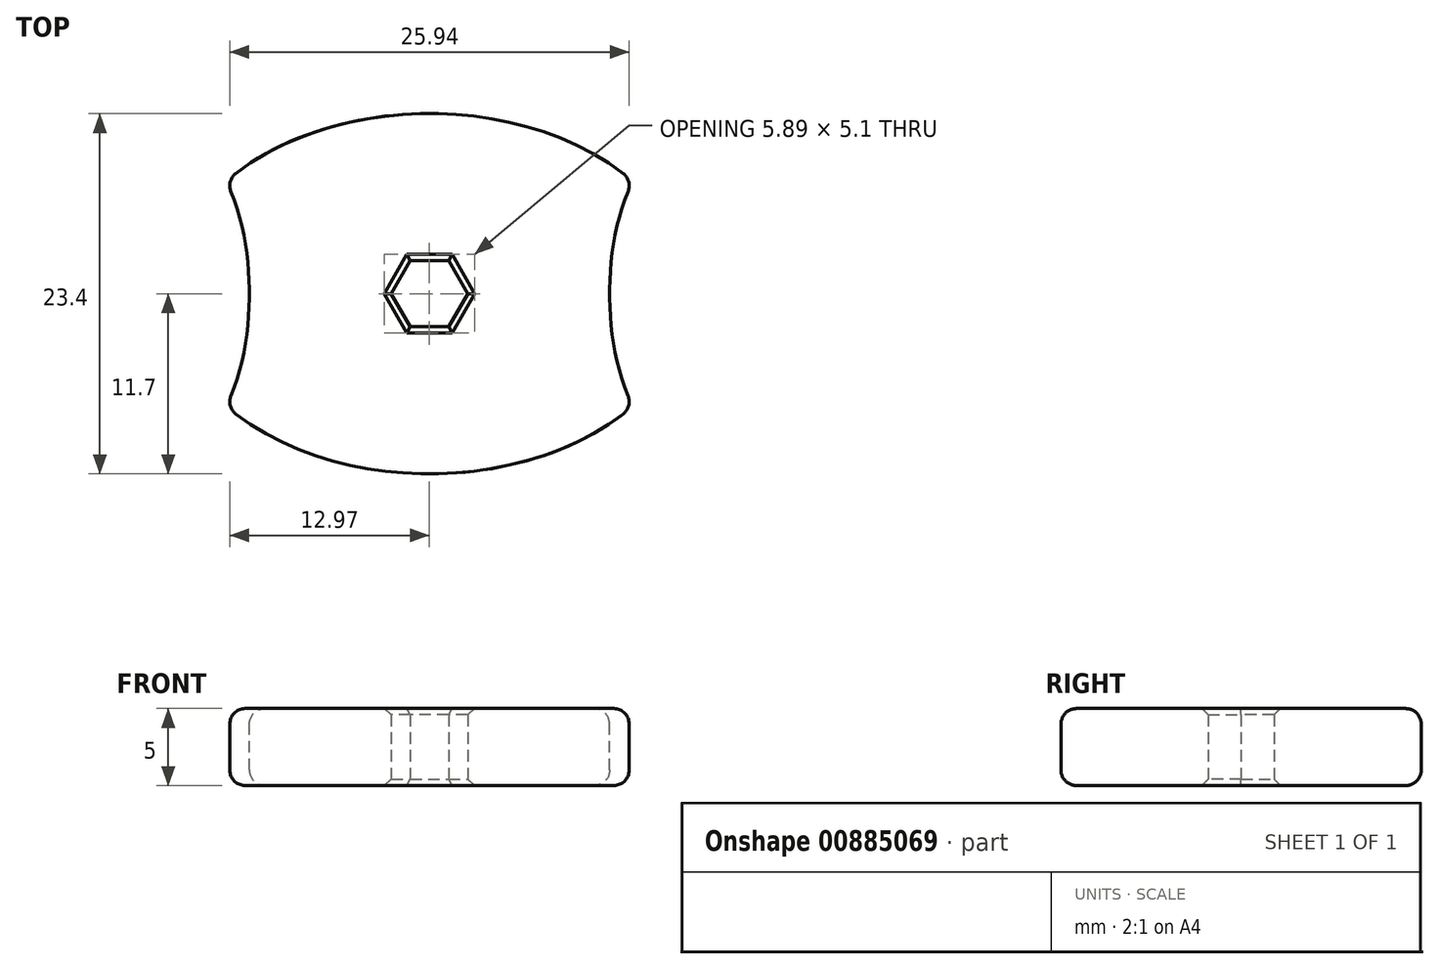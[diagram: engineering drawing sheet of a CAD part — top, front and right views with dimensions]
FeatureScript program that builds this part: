
annotation { "Feature Type Name" : "Feature", "Feature Type Description" : "" }
export const myFeature = defineFeature(function(context is Context, id is Id, definition is map)
    precondition{}
    {
        {
            var Q0;
            Q0=qCreatedBy(makeId("Top.planeOp"),FACE);
            var sketch = newSketch(context, id + "F0", { "sketchPlane" : qUnion([Q0])});
            skCircle(sketch, "E0.cCircle", {"center": v(0, 0) * mm, "radius": 2.15 * mm, "construction": true});
            skLineSegment(sketch, "E0.0", {"start": v(-1.24, 2.15) * mm, "end": v(1.24, 2.15) * mm});
            skLineSegment(sketch, "E0.1", {"start": v(1.24, 2.15) * mm, "end": v(2.48, 0) * mm});
            skLineSegment(sketch, "E0.2", {"start": v(2.48, 0) * mm, "end": v(1.24, -2.15) * mm});
            skLineSegment(sketch, "E0.3", {"start": v(1.24, -2.15) * mm, "end": v(-1.24, -2.15) * mm});
            skLineSegment(sketch, "E0.4", {"start": v(-1.24, -2.15) * mm, "end": v(-2.48, 0) * mm});
            skLineSegment(sketch, "E0.5", {"start": v(-2.48, 0) * mm, "end": v(-1.24, 2.15) * mm});
            skPoint(sketch, "E0.0.midPoint", {"position": v(0, 2.15) * mm});
            skEllipse(sketch, "E1", {"center": v(0, 0) * mm, "majorRadius": 16.9 * mm, "minorRadius": 11.7 * mm, "majorAxis": v(1, 0)});
            skEllipse(sketch, "E2", {"center": v(16.9, 0) * mm, "majorRadius": 10.4 * mm, "minorRadius": 5.2 * mm, "majorAxis": v(0, 1)});
            skEllipse(sketch, "E3.MirrorC", {"center": v(-16.9, 0) * mm, "majorRadius": 10.4 * mm, "minorRadius": 5.2 * mm, "majorAxis": v(0, 1)});
            skSolve(sketch);
        }
        {
            var Q0;
            Q0=makeQuery(id+"F0.imprint","IMPRINT",FACE,{"disambiguationData":[TD([[makeQuery(id+"F0.imprint","IMPRINT",EDGE,{"derivedFrom":sQuery(id+"F0.wireOp",EDGE,"E0.0")}),1.0]])]});
            extrude(context, id + "F1", {"entities" : qUnion([Q0]), "depth" : 5 * mm, "offsetDistance" : 25 * mm});
        }
        {
            var Q0;
            {var subQ0=sQuery(id+"F0.wireOp",EDGE,"E2");var subQ1=sQuery(id+"F0.wireOp",EDGE,"E1");Q0=makeQuery(id+"F1.opExtrude","SWEPT_EDGE",EDGE,{"disambiguationData":[OSD([subQ1,subQ0]),TDD([makeQuery(id+"F0.imprint","INTERSECT",VERTEX,{"disambiguationData":[OD(1.0)],"derivedFrom":[subQ1,subQ0]})])]});}
            var Q1;
            {var subQ0=sQuery(id+"F0.wireOp",EDGE,"E2");var subQ1=sQuery(id+"F0.wireOp",EDGE,"E1");Q1=makeQuery(id+"F1.opExtrude","SWEPT_EDGE",EDGE,{"disambiguationData":[OSD([subQ1,subQ0]),TDD([makeQuery(id+"F0.imprint","INTERSECT",VERTEX,{"disambiguationData":[OD(0.0)],"derivedFrom":[subQ1,subQ0]})])]});}
            var Q2;
            {var subQ0=sQuery(id+"F0.wireOp",EDGE,"E3.MirrorC");var subQ1=sQuery(id+"F0.wireOp",EDGE,"E1");Q2=makeQuery(id+"F1.opExtrude","SWEPT_EDGE",EDGE,{"disambiguationData":[OSD([subQ1,subQ0]),TDD([makeQuery(id+"F0.imprint","INTERSECT",VERTEX,{"disambiguationData":[OD(0.0)],"derivedFrom":[subQ1,subQ0]})])]});}
            var Q3;
            {var subQ0=sQuery(id+"F0.wireOp",EDGE,"E3.MirrorC");var subQ1=sQuery(id+"F0.wireOp",EDGE,"E1");Q3=makeQuery(id+"F1.opExtrude","SWEPT_EDGE",EDGE,{"disambiguationData":[OSD([subQ1,subQ0]),TDD([makeQuery(id+"F0.imprint","INTERSECT",VERTEX,{"disambiguationData":[OD(1.0)],"derivedFrom":[subQ1,subQ0]})])]});}
            fillet(context, id + "F2", {"entities" : qUnion([Q0, Q1, Q2, Q3]), "radius" : 1 * mm, "tangentPropagation" : true, "allowEdgeOverflow" : false});
        }
        {
            var Q0;
            {var subQ0=sQuery(id+"F0.wireOp",EDGE,"E1");Q0=makeQuery(id+"F1.opExtrude","CAP_EDGE",EDGE,{"disambiguationData":[OSD([subQ0]),TDD([makeQuery(id+"F0.imprint","IMPRINT",EDGE,{"disambiguationData":[TD([[makeQuery(id+"F0.imprint","INTERSECT",VERTEX,{"disambiguationData":[OD(1.0)],"derivedFrom":[subQ0,sQuery(id+"F0.wireOp",EDGE,"E3.MirrorC")]}),-1.0]])],"derivedFrom":subQ0})])],"isStart":false});}
            var Q1;
            {var subQ0=sQuery(id+"F0.wireOp",EDGE,"E1");Q1=makeQuery(id+"F1.opExtrude","CAP_EDGE",EDGE,{"disambiguationData":[OSD([subQ0]),TDD([makeQuery(id+"F0.imprint","IMPRINT",EDGE,{"disambiguationData":[TD([[makeQuery(id+"F0.imprint","INTERSECT",VERTEX,{"disambiguationData":[OD(1.0)],"derivedFrom":[subQ0,sQuery(id+"F0.wireOp",EDGE,"E3.MirrorC")]}),-1.0]])],"derivedFrom":subQ0})])],"isStart":true});}
            fillet(context, id + "F3", {"entities" : qUnion([Q0, Q1]), "radius" : 1 * mm, "tangentPropagation" : true, "allowEdgeOverflow" : false});
        }
        {
            var Q0;
            Q0=makeQuery(id+"F1.opExtrude","CAP_EDGE",EDGE,{"disambiguationData":[OSD([sQuery(id+"F0.wireOp",EDGE,"E0.4")])],"isStart":false});
            var Q1;
            Q1=makeQuery(id+"F1.opExtrude","CAP_EDGE",EDGE,{"disambiguationData":[OSD([sQuery(id+"F0.wireOp",EDGE,"E0.3")])],"isStart":false});
            var Q2;
            Q2=makeQuery(id+"F1.opExtrude","CAP_EDGE",EDGE,{"disambiguationData":[OSD([sQuery(id+"F0.wireOp",EDGE,"E0.2")])],"isStart":false});
            var Q3;
            Q3=makeQuery(id+"F1.opExtrude","CAP_EDGE",EDGE,{"disambiguationData":[OSD([sQuery(id+"F0.wireOp",EDGE,"E0.1")])],"isStart":false});
            var Q4;
            Q4=makeQuery(id+"F1.opExtrude","CAP_EDGE",EDGE,{"disambiguationData":[OSD([sQuery(id+"F0.wireOp",EDGE,"E0.0")])],"isStart":false});
            var Q5;
            Q5=makeQuery(id+"F1.opExtrude","CAP_EDGE",EDGE,{"disambiguationData":[OSD([sQuery(id+"F0.wireOp",EDGE,"E0.5")])],"isStart":false});
            var Q6;
            Q6=makeQuery(id+"F1.opExtrude","CAP_EDGE",EDGE,{"disambiguationData":[OSD([sQuery(id+"F0.wireOp",EDGE,"E0.0")])],"isStart":true});
            var Q7;
            Q7=makeQuery(id+"F1.opExtrude","CAP_EDGE",EDGE,{"disambiguationData":[OSD([sQuery(id+"F0.wireOp",EDGE,"E0.5")])],"isStart":true});
            var Q8;
            Q8=makeQuery(id+"F1.opExtrude","CAP_EDGE",EDGE,{"disambiguationData":[OSD([sQuery(id+"F0.wireOp",EDGE,"E0.1")])],"isStart":true});
            var Q9;
            Q9=makeQuery(id+"F1.opExtrude","CAP_EDGE",EDGE,{"disambiguationData":[OSD([sQuery(id+"F0.wireOp",EDGE,"E0.2")])],"isStart":true});
            var Q10;
            Q10=makeQuery(id+"F1.opExtrude","CAP_EDGE",EDGE,{"disambiguationData":[OSD([sQuery(id+"F0.wireOp",EDGE,"E0.3")])],"isStart":true});
            var Q11;
            Q11=makeQuery(id+"F1.opExtrude","CAP_EDGE",EDGE,{"disambiguationData":[OSD([sQuery(id+"F0.wireOp",EDGE,"E0.4")])],"isStart":true});
            chamfer(context, id + "F4", {"entities" : qUnion([Q0, Q1, Q2, Q3, Q4, Q5, Q6, Q7, Q8, Q9, Q10, Q11]), "width" : .4 * mm, "tangentPropagation" : true});
        }
    });
